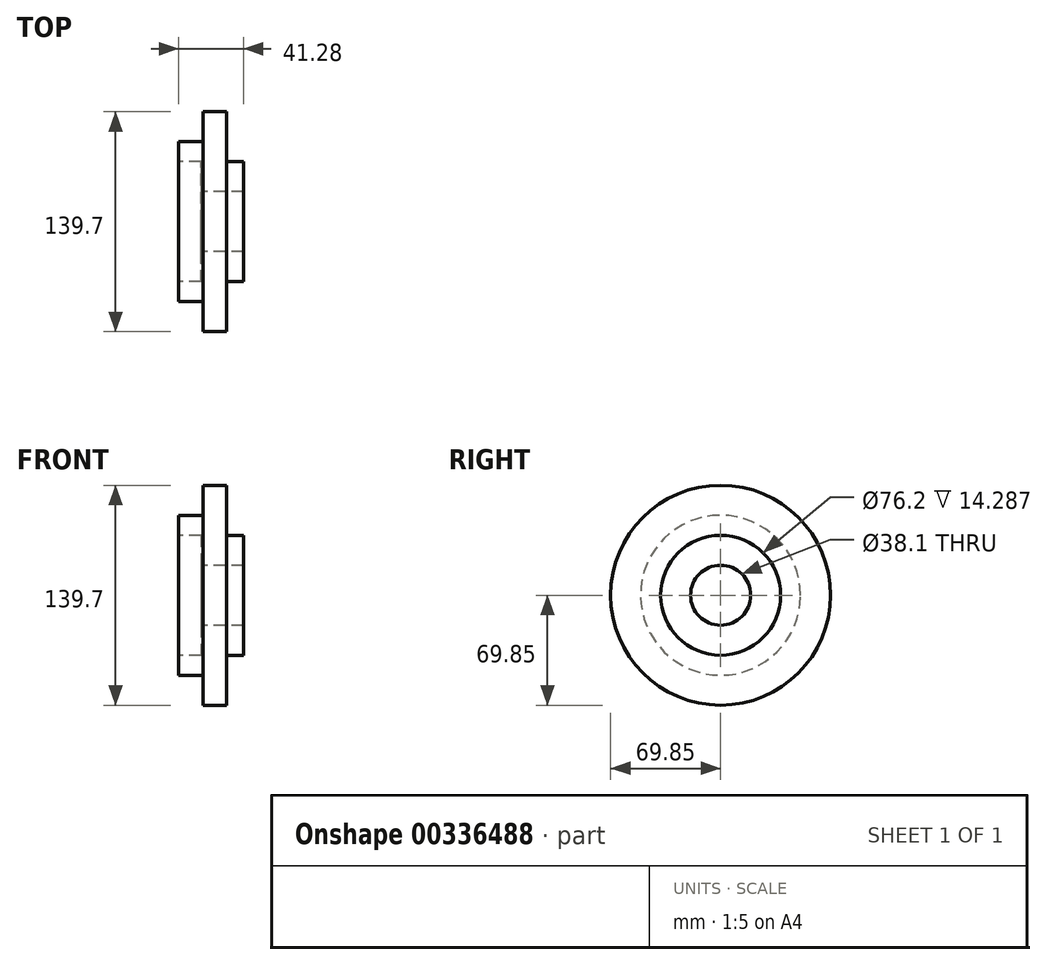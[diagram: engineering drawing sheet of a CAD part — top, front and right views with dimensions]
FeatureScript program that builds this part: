
annotation { "Feature Type Name" : "Feature", "Feature Type Description" : "" }
export const myFeature = defineFeature(function(context is Context, id is Id, definition is map)
    precondition{}
    {
        {
            var Q0;
            Q0=qCreatedBy(makeId("Front.planeOp"),FACE);
            var sketch = newSketch(context, id + "F0", { "sketchPlane" : qUnion([Q0])});
            skLineSegment(sketch, "E0", {"start": v(-90.49, 0) * mm, "end": v(115.89, 0) * mm, "construction": true});
            skLineSegment(sketch, "E1", {"start": v(21.03, 50.8) * mm, "end": v(36.51, 50.8) * mm});
            skLineSegment(sketch, "E2", {"start": v(36.51, 50.8) * mm, "end": v(36.51, 69.85) * mm});
            skLineSegment(sketch, "E3", {"start": v(36.51, 69.85) * mm, "end": v(51.6, 69.85) * mm});
            skLineSegment(sketch, "E4", {"start": v(51.6, 69.85) * mm, "end": v(51.6, 38.1) * mm});
            skLineSegment(sketch, "E5", {"start": v(51.6, 38.1) * mm, "end": v(62.3, 38.1) * mm});
            skLineSegment(sketch, "E6", {"start": v(62.3, 38.1) * mm, "end": v(62.3, 19.05) * mm});
            skLineSegment(sketch, "E7", {"start": v(62.3, 19.05) * mm, "end": v(35.32, 19.05) * mm});
            skLineSegment(sketch, "E8", {"start": v(35.32, 19.05) * mm, "end": v(35.32, 38.1) * mm});
            skLineSegment(sketch, "E9", {"start": v(35.32, 38.1) * mm, "end": v(21.03, 38.1) * mm});
            skLineSegment(sketch, "E10", {"start": v(21.03, 38.1) * mm, "end": v(21.03, 50.8) * mm});
            skSolve(sketch);
        }
        {
            var Q0;
            Q0=makeQuery(id+"F0.imprint","IMPRINT",FACE,{"disambiguationData":[TD([[makeQuery(id+"F0.imprint","IMPRINT",EDGE,{"derivedFrom":sQuery(id+"F0.wireOp",EDGE,"E1")}),-1.0]])]});
            var Q1;
            Q1=sQuery(id+"F0.wireOp",EDGE,"E0");
            revolve(context, id + "F1", {"entities" : qUnion([Q0]), "axis" : qUnion([Q1]), "revolveType" : RevolveType.FULL});
        }
    });
